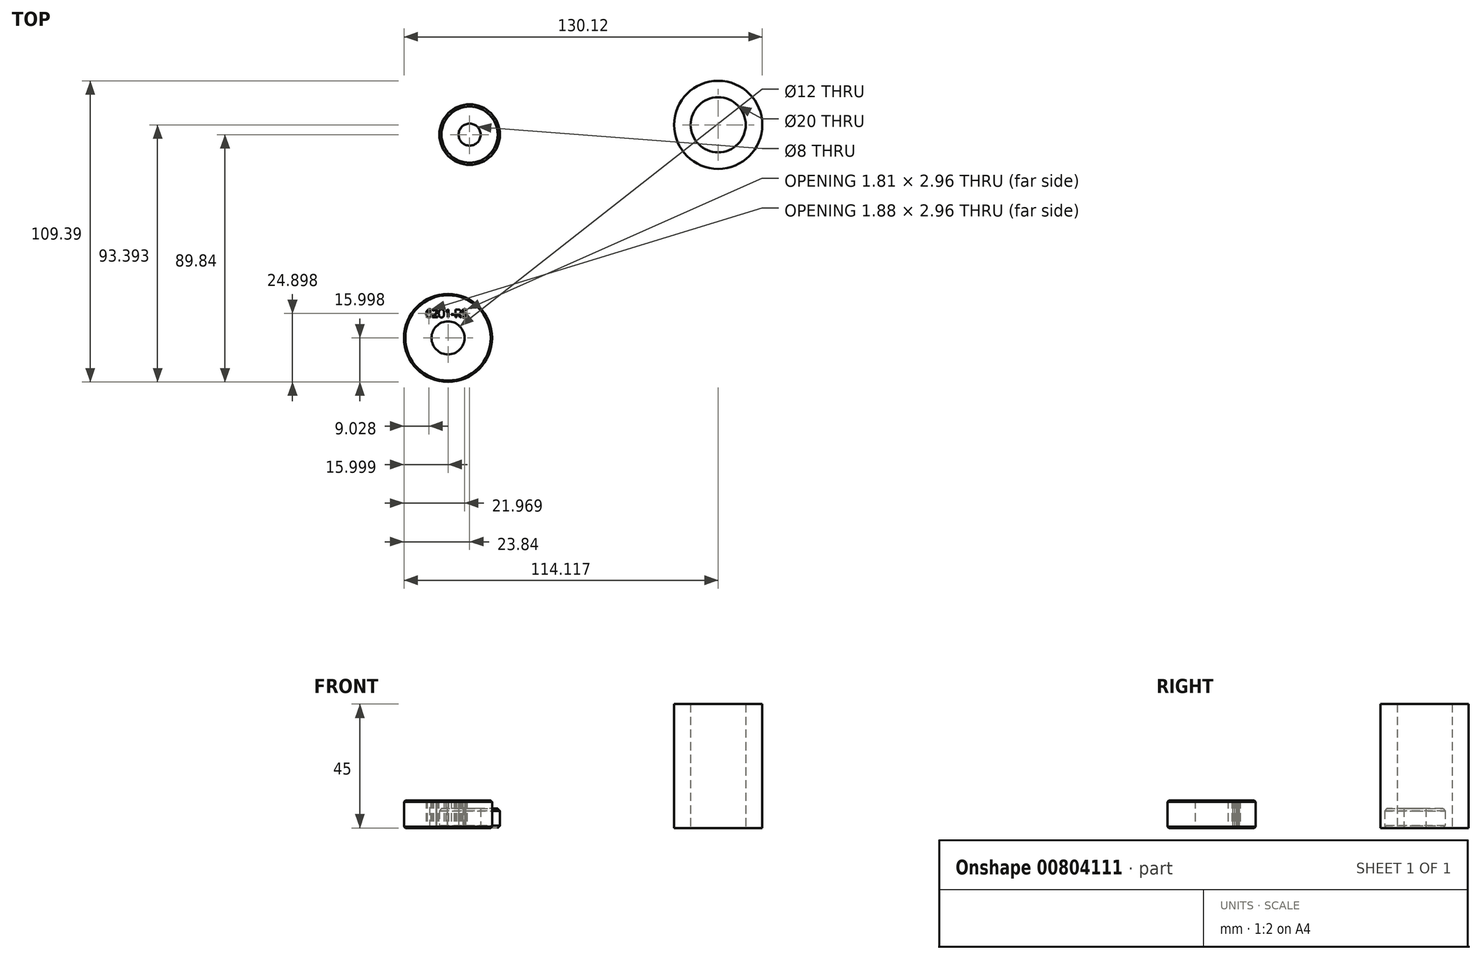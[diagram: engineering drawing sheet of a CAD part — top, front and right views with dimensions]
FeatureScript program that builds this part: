
annotation { "Feature Type Name" : "Feature", "Feature Type Description" : "" }
export const myFeature = defineFeature(function(context is Context, id is Id, definition is map)
    precondition{}
    {
        {
            var Q0;
            Q0=qCreatedBy(makeId("Top.planeOp"),FACE);
            var sketch = newSketch(context, id + "F0", { "sketchPlane" : qUnion([Q0]), "asVersion" : FeatureScriptVersionNumber.V236_DEFAULT_MAX_ASSEMBLIES});
            skCircle(sketch, "E0", {"center": v(-54.52, 42.58) * mm, "radius": 4 * mm});
            skCircle(sketch, "E1", {"center": v(-54.52, 42.58) * mm, "radius": 11 * mm});
            skSolve(sketch);
        }
        {
            var Q0;
            Q0=makeQuery(id+"F0.imprint","IMPRINT",FACE,{"disambiguationData":[TD([[makeQuery(id+"F0.imprint","IMPRINT",EDGE,{"derivedFrom":sQuery(id+"F0.wireOp",EDGE,"E0")}),-1.0]])]});
            extrude(context, id + "F1", {"entities" : qUnion([Q0]), "depth" : 7 * mm});
        }
        {
            var Q0;
            Q0=makeQuery(id+"F1.opExtrude","CAP_EDGE",EDGE,{"disambiguationData":[OSD([sQuery(id+"F0.wireOp",EDGE,"E1")])],"isStart":false});
            var Q1;
            Q1=makeQuery(id+"F1.opExtrude","CAP_EDGE",EDGE,{"disambiguationData":[OSD([sQuery(id+"F0.wireOp",EDGE,"E1")])],"isStart":true});
            chamfer(context, id + "F2", {"entities" : qUnion([Q0, Q1]), "width" : .8 * mm, "tangentPropagation" : true});
        }
        {
            var Q0;
            Q0=qCreatedBy(makeId("Top.planeOp"),FACE);
            var sketch = newSketch(context, id + "F3", { "sketchPlane" : qUnion([Q0]), "asVersion" : FeatureScriptVersionNumber.V236_DEFAULT_MAX_ASSEMBLIES});
            skCircle(sketch, "E2", {"center": v(35.76, 46.13) * mm, "radius": 10 * mm});
            skCircle(sketch, "E3", {"center": v(35.76, 46.13) * mm, "radius": 16 * mm});
            skSolve(sketch);
        }
        {
            var Q0;
            Q0=makeQuery(id+"F3.imprint","IMPRINT",FACE,{"disambiguationData":[TD([[makeQuery(id+"F3.imprint","IMPRINT",EDGE,{"derivedFrom":sQuery(id+"F3.wireOp",EDGE,"E2")}),-1.0]])]});
            extrude(context, id + "F4", {"entities" : qUnion([Q0]), "depth" : 45 * mm});
        }
        {
            var Q0;
            Q0=qCreatedBy(makeId("Top.planeOp"),FACE);
            var sketch = newSketch(context, id + "F5", { "sketchPlane" : qUnion([Q0])});
            skCircle(sketch, "E4", {"center": v(-62.36, -31.26) * mm, "radius": 6 * mm});
            skCircle(sketch, "E5", {"center": v(-62.36, -31.26) * mm, "radius": 16 * mm});
            skText(sketch, "E6", { "text": "6201-RS", "fontName": "OpenSans-Regular.ttf"});
            const initialGuessF5  = {"E6": [-0.0705, -0.0238, 1, 0, 0.0029]};
            skSetInitialGuess(sketch, initialGuessF5);
            skSolve(sketch);
        }
        {
            var Q0;
            Q0=qSketchRegion(id+"F5",true);
            extrude(context, id + "F6", {"entities" : qUnion([Q0]), "depth" : 10 * mm});
        }
        {
            var Q0;
            Q0=makeQuery(id+"F6.opExtrude","CAP_EDGE",EDGE,{"disambiguationData":[OSD([sQuery(id+"F5.wireOp",EDGE,"E5")])],"isStart":false});
            var Q1;
            Q1=makeQuery(id+"F6.opExtrude","CAP_EDGE",EDGE,{"disambiguationData":[OSD([sQuery(id+"F5.wireOp",EDGE,"E5")])],"isStart":true});
            chamfer(context, id + "F7", {"entities" : qUnion([Q0, Q1]), "width" : .5 * mm, "tangentPropagation" : true});
        }
    });
